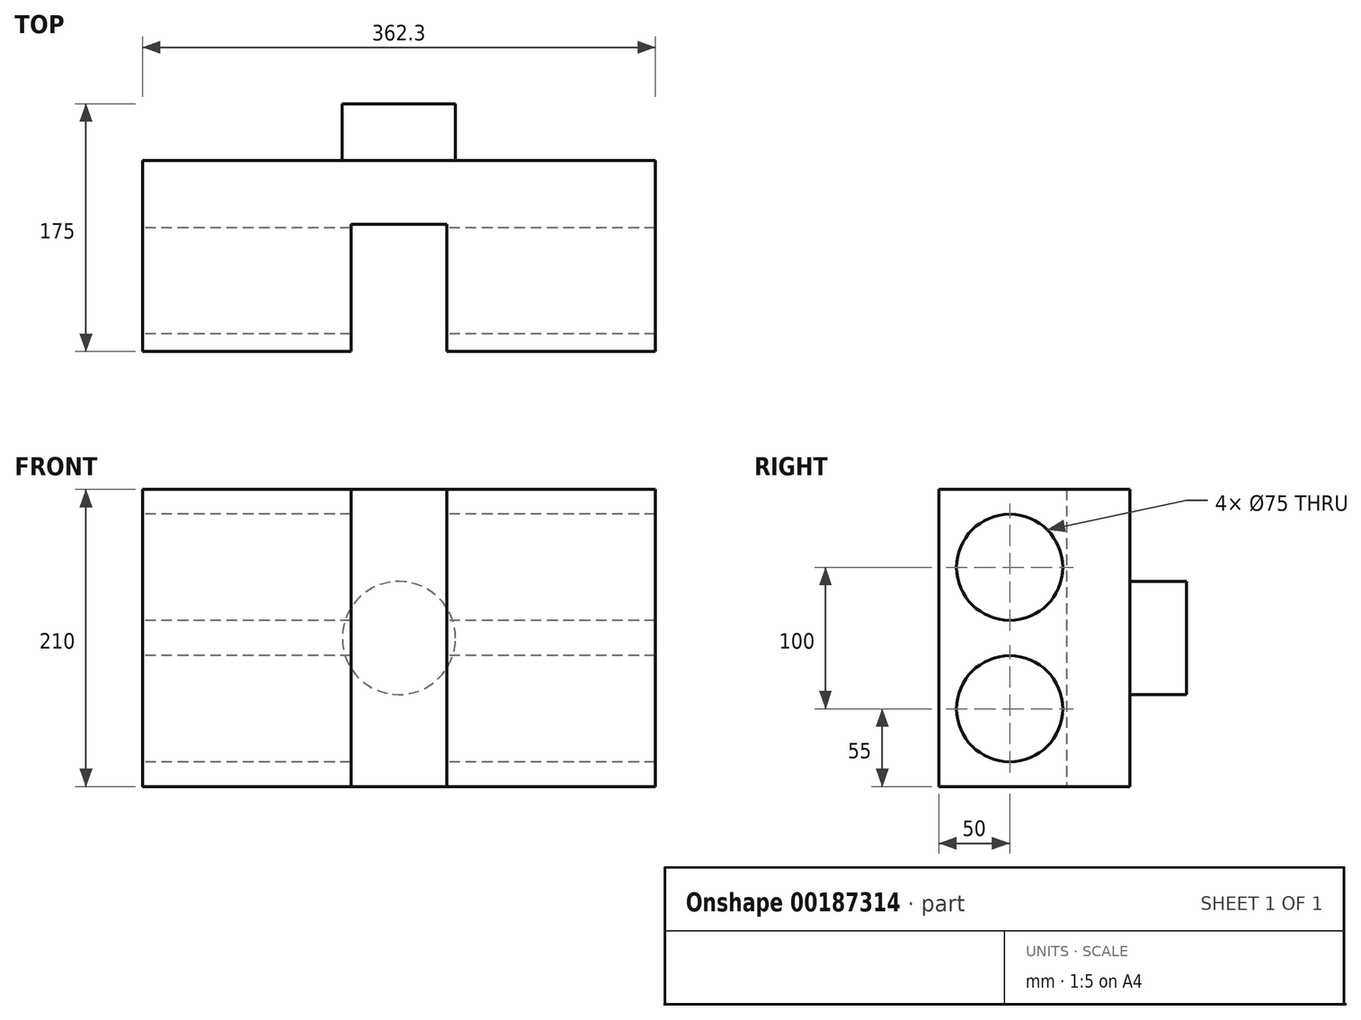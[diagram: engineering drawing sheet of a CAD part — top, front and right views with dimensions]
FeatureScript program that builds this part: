
annotation { "Feature Type Name" : "Feature", "Feature Type Description" : "" }
export const myFeature = defineFeature(function(context is Context, id is Id, definition is map)
    precondition{}
    {
        {
            var Q0;
            Q0=qCreatedBy(makeId("Front.planeOp"),FACE);
            var sketch = newSketch(context, id + "F0", { "sketchPlane" : qUnion([Q0])});
            skLineSegment(sketch, "E0.bottom", {"start": v(181.15, -105) * mm, "end": v(-181.15, -105) * mm});
            skLineSegment(sketch, "E0.top", {"start": v(181.15, 105) * mm, "end": v(-181.15, 105) * mm});
            skLineSegment(sketch, "E0.left", {"start": v(181.15, -105) * mm, "end": v(181.15, 105) * mm});
            skLineSegment(sketch, "E0.right", {"start": v(-181.15, -105) * mm, "end": v(-181.15, 105) * mm});
            skPoint(sketch, "E0.middle", {"position": v(0, 0) * mm});
            skSolve(sketch);
        }
        {
            var Q0;
            Q0 = qSketchRegion(id + "F0", true);
            extrude(context, id + "F1", {"entities" : qUnion([Q0]), "oppositeDirection" : true, "depth" : 135 * mm});
        }
        {
            var Q0;
            Q0=makeQuery(id+"F1.opExtrude","CAP_FACE",FACE,{"disambiguationData":[OSD([sQuery(id+"F0.wireOp",EDGE,"E0.bottom"),sQuery(id+"F0.wireOp",EDGE,"E0.top"),sQuery(id+"F0.wireOp",EDGE,"E0.left"),sQuery(id+"F0.wireOp",EDGE,"E0.right")])],"isStart":false});
            var sketch = newSketch(context, id + "F2", { "sketchPlane" : qUnion([Q0])});
            skCircle(sketch, "E1", {"center": v(0, 0) * mm, "radius": 40 * mm});
            skSolve(sketch);
        }
        {
            var Q0;
            Q0 = qSketchRegion(id + "F2", true);
            extrude(context, id + "F3", {"entities" : qUnion([Q0]), "operationType" : NewBodyOperationType.ADD, "depth" : 40 * mm});
        }
        {
            var Q0;
            Q0=makeQuery(id+"F1.opExtrude","SWEPT_FACE",FACE,{"disambiguationData":[OSD([sQuery(id+"F0.wireOp",EDGE,"E0.bottom")])]});
            var sketch = newSketch(context, id + "F4", { "sketchPlane" : qUnion([Q0])});
            skLineSegment(sketch, "E2", {"start": v(-33.8, 0) * mm, "end": v(0, 0) * mm});
            skLineSegment(sketch, "E3", {"start": v(-33.8, 0) * mm, "end": v(-33.8, -90) * mm});
            skLineSegment(sketch, "E4", {"start": v(-33.8, -90) * mm, "end": v(-73.8, -90) * mm});
            skLineSegment(sketch, "E5", {"start": v(-73.8, -90) * mm, "end": v(-73.8, 0) * mm});
            skLineSegment(sketch, "E6", {"start": v(-73.8, 0) * mm, "end": v(-181.15, 0) * mm});
            skLineSegment(sketch, "E7.MirrorCS", {"start": v(33.8, 0) * mm, "end": v(0, 0) * mm});
            skLineSegment(sketch, "E8.MirrorCS", {"start": v(33.8, -90) * mm, "end": v(73.8, -90) * mm});
            skLineSegment(sketch, "E9.MirrorCS", {"start": v(73.8, -90) * mm, "end": v(73.8, 0) * mm});
            skLineSegment(sketch, "E10.MirrorCS", {"start": v(33.8, 0) * mm, "end": v(33.8, -90) * mm});
            skLineSegment(sketch, "E11.MirrorCS", {"start": v(73.8, 0) * mm, "end": v(181.15, 0) * mm});
            skLineSegment(sketch, "E12", {"start": v(33.8, -90) * mm, "end": v(-33.8, -90) * mm});
            skSolve(sketch);
        }
        {
            var Q0;
            Q0=makeQuery(id+"F4.imprint","IMPRINT",FACE,{"disambiguationData":[TD([[makeQuery(id+"F4.imprint","IMPRINT",EDGE,{"derivedFrom":sQuery(id+"F4.wireOp",EDGE,"E2")}),1.0]])]});
            extrude(context, id + "F5", {"entities" : qUnion([Q0]), "operationType" : NewBodyOperationType.REMOVE, "endBound" : BoundingType.THROUGH_ALL, "oppositeDirection" : true, "depth" : 25 * mm});
        }
        {
            var Q0;
            Q0=makeQuery(id+"F1.opExtrude","SWEPT_FACE",FACE,{"disambiguationData":[OSD([sQuery(id+"F0.wireOp",EDGE,"E0.right")])]});
            var sketch = newSketch(context, id + "F6", { "sketchPlane" : qUnion([Q0])});
            skCircle(sketch, "E13", {"center": v(-50, 50) * mm, "radius": 37.5 * mm});
            skCircle(sketch, "E14", {"center": v(-50, -50) * mm, "radius": 37.5 * mm});
            skLineSegment(sketch, "E15", {"start": v(-50, 105) * mm, "end": v(-50, -105) * mm, "construction": true});
            skLineSegment(sketch, "E16", {"start": v(-50, -50) * mm, "end": v(-50, -105) * mm, "construction": true});
            skLineSegment(sketch, "E17", {"start": v(-50, 50) * mm, "end": v(-50, 105) * mm, "construction": true});
            skSolve(sketch);
        }
        {
            var Q0;
            Q0 = qSketchRegion(id + "F6", true);
            extrude(context, id + "F7", {"entities" : qUnion([Q0]), "operationType" : NewBodyOperationType.REMOVE, "endBound" : BoundingType.THROUGH_ALL, "oppositeDirection" : true, "depth" : 25 * mm});
        }
    });
